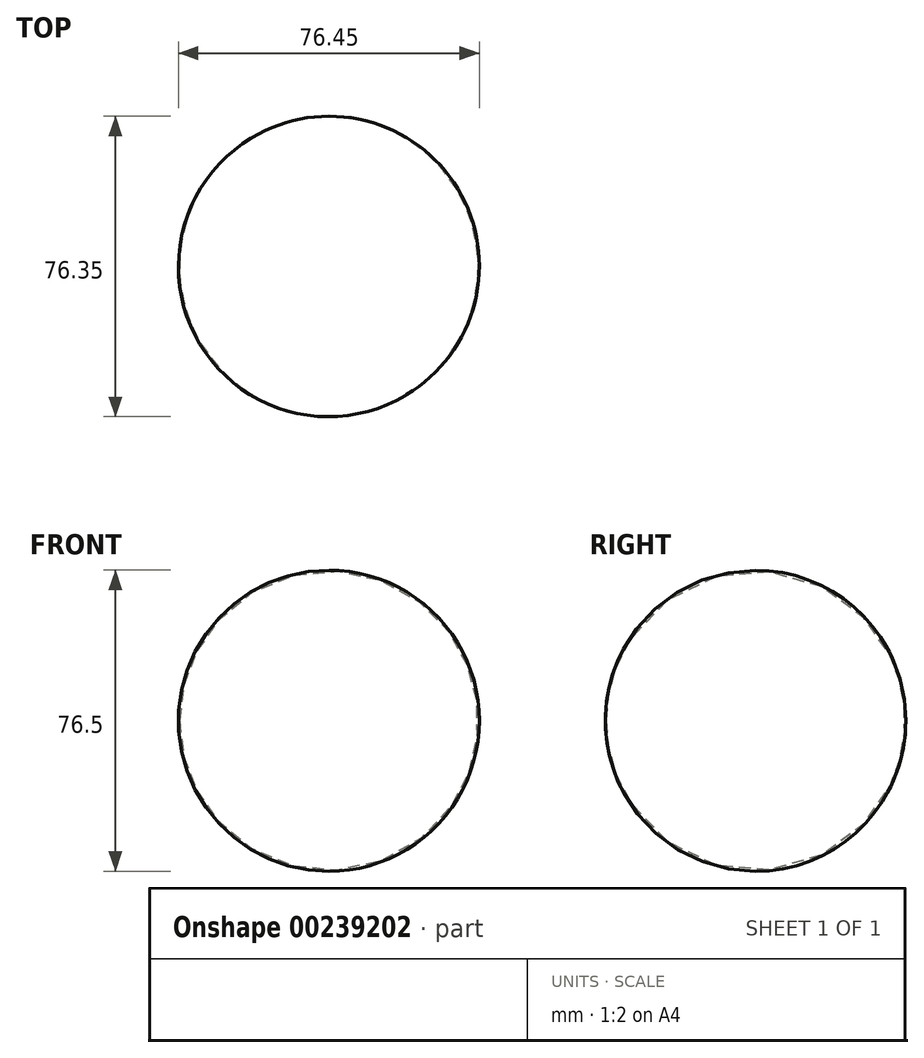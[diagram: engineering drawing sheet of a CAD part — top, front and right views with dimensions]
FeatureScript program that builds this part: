
annotation { "Feature Type Name" : "Feature", "Feature Type Description" : "" }
export const myFeature = defineFeature(function(context is Context, id is Id, definition is map)
    precondition{}
    {
        {
            var Q0;
            Q0=qCreatedBy(makeId("Top.planeOp"),FACE);
            var sketch = newSketch(context, id + "F0", { "sketchPlane" : qUnion([Q0])});
            skCircle(sketch, "E0", {"center": v(0, 0) * mm, "radius": 38.1 * mm});
            skLineSegment(sketch, "E1", {"start": v(19.74, -32.59) * mm, "end": v(-19.49, 32.74) * mm});
            skSolve(sketch);
        }
        {
            var Q0;
            {var subQ0=sQuery(id+"F0.wireOp",EDGE,"E1");Q0=makeQuery(id+"F0.imprint","IMPRINT",FACE,{"disambiguationData":[TD([[makeQuery(id+"F0.imprint","IMPRINT",EDGE,{"derivedFrom":subQ0}),-1.0]])]});}
            var Q1;
            Q1=sQuery(id+"F0.wireOp",EDGE,"E1");
            revolve(context, id + "F1", {"entities" : qUnion([Q0]), "axis" : qUnion([Q1]), "revolveType" : RevolveType.ONE_DIRECTION, "angle" : 360 * degree});
        }
    });
